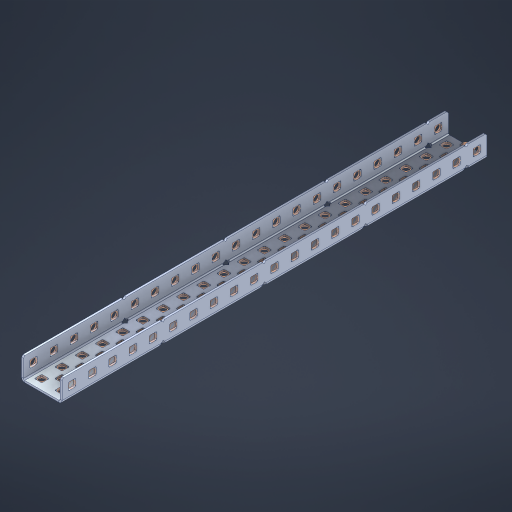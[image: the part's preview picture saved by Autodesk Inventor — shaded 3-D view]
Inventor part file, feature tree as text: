
AUTODESK INVENTOR PART (.ipt)
format: ipt  version: 2023 (Build 270158000, 158)  size: 1,467,392 bytes
history: native  units: in
note: dims shown in document units (in); Inventor stores cm internally (conversion verified against a paired STEP export)
features: other x112, extrude x103, sheet_metal_op x11, sketch x10, pattern_linear x2, mirror x1, chamfer x1
ambient origin geometry x8: Origin, YZ Plane, XZ Plane, XY Plane, X Axis, Y Axis, Z Axis, Center Point
bodies: Solid1 (feature_tree), Body (feature_tree)
feature tree (240):
  sheet_metal_op  "Flanges"
  other  "Flange Pattern Plane"
  other  "Flange Pattern Sketch"
  sheet_metal_op  "Flange Pattern"
  sheet_metal_op  "Body Pattern"
  pattern_linear  "Center Pattern"  Spacing1=0.0469in  [1 undecoded]
  other  "Arc Length"
  mirror  "Notch Mirror"
  pattern_linear  "Notch Pattern"  Spacing1=0.182in  [1 undecoded]
  chamfer  "End Chamfer"
  extrude  "Half Cut"  Depth=0.02in
  sketch  "Sketch1"  dims[d0=1.0in]
  other  "Plate1"
  sketch  "Sketch2"  dims[d1=10.5in]
  other  "Plate2"
  sheet_metal_op  "Bend1"
  sheet_metal_op  "Corner1"
  sketch  "Sketch3"  dims[d2=0.0469in]
  sketch  "Sketch7"  dims[d3=0.0469in]
  other  "Srf1"
  other  "Srf2"
  sketch  "Sketch8"  dims[d4=0.0234in]
  sketch  "Sketch9"  dims[d5=0.0938in]
  other  "Srf91"
  sheet_metal_op  "Body Pattern Sketch"
  other  "Srf92"
  sketch  "Sketch13"  dims[d6=0.0469in]
  sketch  "Sketch14"  dims[d7=0.5in d8=90.0deg d9=0.0312in]
  sketch  "Sketch15"  dims[d10=0.1875in]
  sketch  "Sketch16"  dims[d11=0.0469in d12=0.0469in d16=0.182in d17=0.02in d18=0.0469in d19=0.0in d20=0.25in d21=0.25in d38=8.2677in d40=0.5in d41=0.7874in d43=1.0in d46=0.172in d47=1.0in d48=0.0in d49=0.182in d50=0.02in d51=0.25in d52=0.25in d53=0.0469in d54=0.0in d55=0.172in d56=1.0in d57=0.0in d58=0.25in d60=8.2677in d62=0.5in d63=0.7874in d65=0.5in d85=0.1227in d86=0.1659in d88=0.04in d89=0.0469in d90=0.0in d91=0.04in d92=0.0491in d95=2.5in d96=0.04in d97=0.25in d98=45.0deg d99=0.25in d100=0.5in d101=0.0in d102=2.497in d106=0.182in d107=0.02in d108=0.5in d109=0.5in d110=0.0469in d111=0.0in d112=0.172in d113=0.5in d114=0.0in d117=0.5in d118=0.5in d119=0.5in]
  other  "Srf786"
  other  "Srf823"
  other  "Srf824"
  other  "Srf825"
  other  "Srf826"
  other  "Srf827"
  other  "Srf828"
  other  "Srf829"
  other  "Srf856"
  other  "Srf857"
  other  "Srf858"
  other  "Srf859"
  other  "Srf860"
  other  "Srf861"
  other  "Srf862"
  other  "Srf889"
  other  "Srf890"
  other  "Srf891"
  other  "Srf892"
  other  "Srf893"
  other  "Srf894"
  other  "Srf895"
  other  "Srf896"
  other  "Srf922"
  other  "Srf923"
  other  "Srf924"
  other  "Srf925"
  other  "Srf926"
  other  "Srf959"
  other  "Srf960"
  other  "Srf961"
  other  "Srf962"
  other  "Srf963"
  other  "Srf996"
  other  "Srf997"
  other  "Srf998"
  other  "Srf999"
  other  "Srf1000"
  other  "Srf1143"
  other  "Srf1144"
  other  "Srf1145"
  other  "Srf1146"
  other  "Srf1147"
  other  "Srf1148"
  other  "Srf1149"
  other  "Srf1150"
  other  "Srf1151"
  other  "Srf1152"
  other  "Srf1153"
  other  "Srf1154"
  other  "Srf1155"
  other  "Srf1156"
  other  "Srf1157"
  other  "Srf1158"
  other  "Srf1159"
  other  "Srf1160"
  other  "Srf1161"
  other  "Srf1162"
  other  "Srf1163"
  other  "Srf1164"
  other  "Srf1165"
  other  "Srf1166"
  other  "Srf1167"
  other  "Srf1168"
  other  "Srf1169"
  other  "Srf1170"
  other  "Srf1199"
  other  "Srf1200"
  other  "Srf1201"
  other  "Srf1202"
  other  "Srf1203"
  other  "Srf1204"
  other  "Srf1205"
  other  "Srf1206"
  other  "Srf1207"
  other  "Srf1208"
  other  "Srf1209"
  other  "Srf1210"
  other  "Srf1211"
  other  "Srf1212"
  other  "Srf1213"
  other  "Srf1214"
  other  "Srf1215"
  other  "Srf1216"
  other  "Srf1217"
  other  "Srf1218"
  other  "Srf1219"
  other  "Srf1220"
  other  "Srf1221"
  other  "Srf1222"
  other  "Srf1223"
  other  "Srf1224"
  other  "Srf1225"
  other  "Srf1226"
  other  "Srf1255"
  other  "Srf1256"
  other  "Srf1257"
  other  "Srf1258"
  other  "Srf1259"
  other  "Srf1260"
  other  "Srf1261"
  sheet_metal_op  "Flange Stamp"
  sheet_metal_op  "Flange Circle"
  sheet_metal_op  "Body Stamp"
  sheet_metal_op  "Body Circle"
  other  "Center Stamp"
  other  "Center Circle"
  sheet_metal_op  "Notch"
  extrude  "ExtrusionSrf2"  Depth=0.0469in
  extrude  "ExtrusionSrf92"  TaperAngle=0.0deg  [1 undecoded]
  extrude  "ExtrusionSrf823"  Depth=0.5in
  extrude  "ExtrusionSrf824"  Depth=0.5in
  extrude  "ExtrusionSrf825"  Depth=0.5in
  extrude  "ExtrusionSrf826"  Depth=0.5in
  extrude  "ExtrusionSrf827"  Depth=1.0in TaperAngle=0.0deg
  extrude  "ExtrusionSrf828"  Depth=0.5in
  extrude  "ExtrusionSrf829"  Depth=0.02in
  extrude  "ExtrusionSrf856"  Depth=0.5in
  extrude  "ExtrusionSrf857"  Depth=0.5in
  extrude  "ExtrusionSrf858"  Depth=0.0469in
  extrude  "ExtrusionSrf859"  TaperAngle=0.0deg  [1 undecoded]
  extrude  "ExtrusionSrf860"  Depth=0.5in
  extrude  "ExtrusionSrf861"  Depth=1.0in TaperAngle=0.0deg
  extrude  "ExtrusionSrf862"  Depth=0.5in
  extrude  "ExtrusionSrf889"  Depth=0.5in
  extrude  "ExtrusionSrf890"  Depth=0.5in
  extrude  "ExtrusionSrf891"  Depth=0.5in
  extrude  "ExtrusionSrf892"  Depth=0.5in
  extrude  "ExtrusionSrf893"  Depth=0.5in
  extrude  "ExtrusionSrf894"  Depth=0.0469in
  extrude  "ExtrusionSrf895"  TaperAngle=0.0deg  [1 undecoded]
  extrude  "ExtrusionSrf896"  Depth=0.5in
  extrude  "ExtrusionSrf922"  Depth=0.5in
  extrude  "ExtrusionSrf923"  Depth=2.5in
  extrude  "ExtrusionSrf924"  Depth=0.5in TaperAngle=45.0deg
  extrude  "ExtrusionSrf925"  Depth=0.5in
  extrude  "ExtrusionSrf926"  Depth=0.5in TaperAngle=0.0deg
  extrude  "ExtrusionSrf959"  Depth=0.5in
  extrude  "ExtrusionSrf960"  Depth=0.5in
  extrude  "ExtrusionSrf961"  Depth=0.02in
  extrude  "ExtrusionSrf962"  Depth=0.5in
  extrude  "ExtrusionSrf963"  Depth=0.5in
  extrude  "ExtrusionSrf996"  Depth=0.0469in
  extrude  "ExtrusionSrf997"  TaperAngle=0.0deg  [1 undecoded]
  extrude  "ExtrusionSrf998"  Depth=0.5in
  extrude  "ExtrusionSrf999"  Depth=0.5in TaperAngle=0.0deg
  extrude  "ExtrusionSrf1000"  Depth=0.5in
  extrude  "ExtrusionSrf1143"  Depth=0.5in
  extrude  "ExtrusionSrf1144"  Depth=0.5in
  extrude  "ExtrusionSrf1145"  [1 undecoded]
  extrude  "ExtrusionSrf1146"  [1 undecoded]
  extrude  "ExtrusionSrf1147"  [1 undecoded]
  extrude  "ExtrusionSrf1148"  [1 undecoded]
  extrude  "ExtrusionSrf1149"  [1 undecoded]
  extrude  "ExtrusionSrf1150"  [1 undecoded]
  extrude  "ExtrusionSrf1151"  [1 undecoded]
  extrude  "ExtrusionSrf1152"  [1 undecoded]
  extrude  "ExtrusionSrf1153"  [1 undecoded]
  extrude  "ExtrusionSrf1154"  [1 undecoded]
  extrude  "ExtrusionSrf1155"  [1 undecoded]
  extrude  "ExtrusionSrf1156"  [1 undecoded]
  extrude  "ExtrusionSrf1157"  [1 undecoded]
  extrude  "ExtrusionSrf1158"  [1 undecoded]
  extrude  "ExtrusionSrf1159"  [1 undecoded]
  extrude  "ExtrusionSrf1160"  [1 undecoded]
  extrude  "ExtrusionSrf1161"  [1 undecoded]
  extrude  "ExtrusionSrf1162"  [1 undecoded]
  extrude  "ExtrusionSrf1163"  [1 undecoded]
  extrude  "ExtrusionSrf1164"  [1 undecoded]
  extrude  "ExtrusionSrf1165"  [1 undecoded]
  extrude  "ExtrusionSrf1166"  [1 undecoded]
  extrude  "ExtrusionSrf1167"  [1 undecoded]
  extrude  "ExtrusionSrf1168"  [1 undecoded]
  extrude  "ExtrusionSrf1169"  [1 undecoded]
  extrude  "ExtrusionSrf1170"  [1 undecoded]
  extrude  "ExtrusionSrf1199"  [1 undecoded]
  extrude  "ExtrusionSrf1200"  [1 undecoded]
  extrude  "ExtrusionSrf1201"  [1 undecoded]
  extrude  "ExtrusionSrf1202"  [1 undecoded]
  extrude  "ExtrusionSrf1203"  [1 undecoded]
  extrude  "ExtrusionSrf1204"  [1 undecoded]
  extrude  "ExtrusionSrf1205"  [1 undecoded]
  extrude  "ExtrusionSrf1206"  [1 undecoded]
  extrude  "ExtrusionSrf1207"  [1 undecoded]
  extrude  "ExtrusionSrf1208"  [1 undecoded]
  extrude  "ExtrusionSrf1209"  [1 undecoded]
  extrude  "ExtrusionSrf1210"  [1 undecoded]
  extrude  "ExtrusionSrf1211"  [1 undecoded]
  extrude  "ExtrusionSrf1212"  [1 undecoded]
  extrude  "ExtrusionSrf1213"  [1 undecoded]
  extrude  "ExtrusionSrf1214"  [1 undecoded]
  extrude  "ExtrusionSrf1215"  [1 undecoded]
  extrude  "ExtrusionSrf1216"  [1 undecoded]
  extrude  "ExtrusionSrf1217"  [1 undecoded]
  extrude  "ExtrusionSrf1218"  [1 undecoded]
  extrude  "ExtrusionSrf1219"  [1 undecoded]
  extrude  "ExtrusionSrf1220"  [1 undecoded]
  extrude  "ExtrusionSrf1221"  [1 undecoded]
  extrude  "ExtrusionSrf1222"  [1 undecoded]
  extrude  "ExtrusionSrf1223"  [1 undecoded]
  extrude  "ExtrusionSrf1224"  [1 undecoded]
  extrude  "ExtrusionSrf1225"  [1 undecoded]
  extrude  "ExtrusionSrf1226"  [1 undecoded]
  extrude  "ExtrusionSrf1255"  [1 undecoded]
  extrude  "ExtrusionSrf1256"  [1 undecoded]
  extrude  "ExtrusionSrf1257"  [1 undecoded]
  extrude  "ExtrusionSrf1258"  [1 undecoded]
  extrude  "ExtrusionSrf1259"  [1 undecoded]
  extrude  "ExtrusionSrf1260"  [1 undecoded]
  extrude  "ExtrusionSrf1261"  [1 undecoded]
note: 67 required parameter values undecoded (feature->parameter linkage not recoverable at this tier; creation-order binding heuristic only, values carry confidence <= 0.55)
